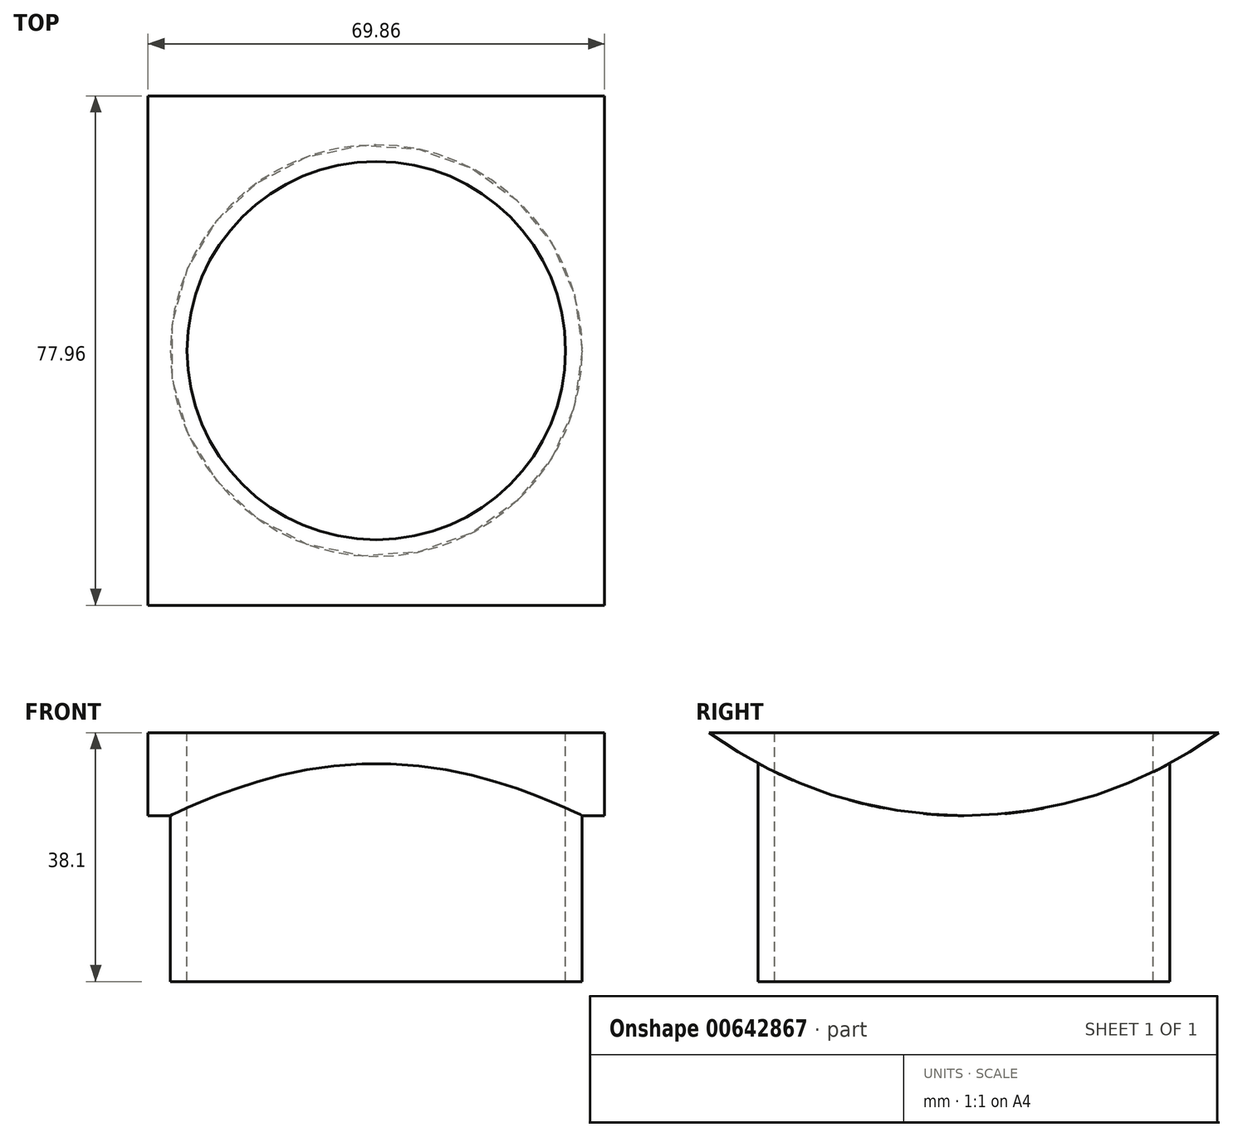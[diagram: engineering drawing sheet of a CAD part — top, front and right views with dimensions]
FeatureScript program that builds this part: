
annotation { "Feature Type Name" : "Feature", "Feature Type Description" : "" }
export const myFeature = defineFeature(function(context is Context, id is Id, definition is map)
    precondition{}
    {
        {
            var Q0;
            Q0=qCreatedBy(makeId("Top.planeOp"),FACE);
            var sketch = newSketch(context, id + "F0", { "sketchPlane" : qUnion([Q0])});
            skCircle(sketch, "E0", {"center": v(0, 0) * mm, "radius": 28.96 * mm});
            skCircle(sketch, "E1", {"center": v(0, 0) * mm, "radius": 31.5 * mm});
            skSolve(sketch);
        }
        {
            var Q0;
            Q0 = qSketchRegion(id + "F0", true);
            extrude(context, id + "F1", {"entities" : qUnion([Q0]), "oppositeDirection" : true, "depth" : 25.4 * mm, "offsetDistance" : 25.4 * mm, "hasSecondDirection" : true, "secondDirectionOppositeDirection" : false, "secondDirectionDepth" : 12.7 * mm});
        }
        {
            var Q0;
            Q0=qCreatedBy(makeId("Right.planeOp"),FACE);
            var sketch = newSketch(context, id + "F2", { "sketchPlane" : qUnion([Q0])});
            skLineSegment(sketch, "E2", {"start": v(0, 0) * mm, "end": v(0, 66.17) * mm, "construction": true});
            skArc(sketch, "E3", {"start": v(0, 0) * mm, "mid": v(-20.5, 3.26) * mm, "end": v(-38.98, 12.7) * mm});
            skArc(sketch, "E4", {"start": v(0, 0) * mm, "mid": v(20.5, 3.26) * mm, "end": v(38.98, 12.7) * mm});
            skLineSegment(sketch, "E5", {"start": v(-38.98, 12.7) * mm, "end": v(38.98, 12.7) * mm});
            skSolve(sketch);
        }
        {
            var Q0;
            Q0 = qSketchRegion(id + "F2", true);
            extrude(context, id + "F3", {"entities" : qUnion([Q0]), "operationType" : NewBodyOperationType.ADD, "depth" : 34.92 * mm, "offsetDistance" : 25.4 * mm, "hasSecondDirection" : true, "secondDirectionOppositeDirection" : true, "secondDirectionDepth" : 34.92 * mm});
        }
        {
            var Q0;
            Q0=makeQuery(id+"F0.imprint","IMPRINT",FACE,{"disambiguationData":[TD([[makeQuery(id+"F0.imprint","IMPRINT",EDGE,{"derivedFrom":sQuery(id+"F0.wireOp",EDGE,"E0")}),1.0]])]});
            extrude(context, id + "F4", {"entities" : qUnion([Q0]), "operationType" : NewBodyOperationType.REMOVE, "depth" : 25.4 * mm, "offsetDistance" : 25.4 * mm});
        }
    });
